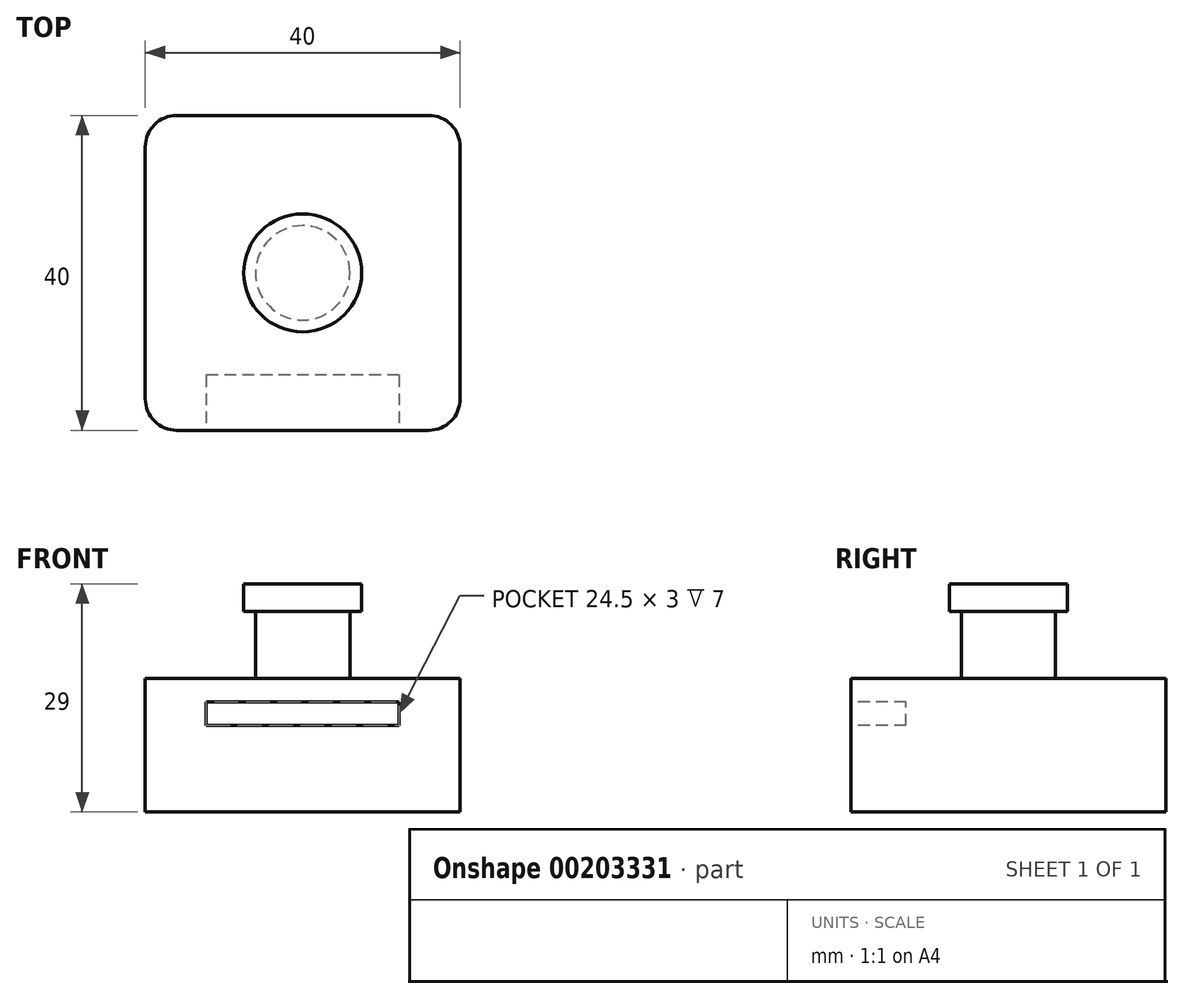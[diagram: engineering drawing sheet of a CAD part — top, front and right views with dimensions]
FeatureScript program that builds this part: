
annotation { "Feature Type Name" : "Feature", "Feature Type Description" : "" }
export const myFeature = defineFeature(function(context is Context, id is Id, definition is map)
    precondition{}
    {
        {
            var Q0;
            Q0=qCreatedBy(makeId("Top.planeOp"),FACE);
            var sketch = newSketch(context, id + "F0", { "sketchPlane" : qUnion([Q0])});
            skLineSegment(sketch, "E0.bottom", {"start": v(20, -20) * mm, "end": v(-20, -20) * mm});
            skLineSegment(sketch, "E0.top", {"start": v(20, 20) * mm, "end": v(-20, 20) * mm});
            skLineSegment(sketch, "E0.left", {"start": v(20, -20) * mm, "end": v(20, 20) * mm});
            skLineSegment(sketch, "E0.right", {"start": v(-20, -20) * mm, "end": v(-20, 20) * mm});
            skPoint(sketch, "E0.middle", {"position": v(0, 0) * mm});
            skSolve(sketch);
        }
        {
            var Q0;
            Q0 = qSketchRegion(id + "F0", true);
            extrude(context, id + "F1", {"entities" : qUnion([Q0]), "oppositeDirection" : true, "depth" : 17 * mm});
        }
        {
            var Q0;
            Q0=makeQuery(id+"F1.opExtrude","CAP_FACE",FACE,{"disambiguationData":[OSD([sQuery(id+"F0.wireOp",EDGE,"E0.bottom"),sQuery(id+"F0.wireOp",EDGE,"E0.top"),sQuery(id+"F0.wireOp",EDGE,"E0.left"),sQuery(id+"F0.wireOp",EDGE,"E0.right")])],"isStart":true});
            var sketch = newSketch(context, id + "F2", { "sketchPlane" : qUnion([Q0])});
            skCircle(sketch, "E1", {"center": v(0, 0) * mm, "radius": 6 * mm});
            skSolve(sketch);
        }
        {
            var Q0;
            Q0 = qSketchRegion(id + "F2", true);
            extrude(context, id + "F3", {"entities" : qUnion([Q0]), "operationType" : NewBodyOperationType.ADD, "depth" : 8.5 * mm});
        }
        {
            var Q0;
            Q0=makeQuery(id+"F3.opExtrude","CAP_FACE",FACE,{"disambiguationData":[OSD([sQuery(id+"F2.wireOp",EDGE,"E1")])],"isStart":false});
            var sketch = newSketch(context, id + "F4", { "sketchPlane" : qUnion([Q0])});
            skCircle(sketch, "E2", {"center": v(0, 0) * mm, "radius": 7.5 * mm});
            skSolve(sketch);
        }
        {
            var Q0;
            Q0 = qSketchRegion(id + "F4", true);
            extrude(context, id + "F5", {"entities" : qUnion([Q0]), "operationType" : NewBodyOperationType.ADD, "depth" : 3.5 * mm});
        }
        {
            var Q0;
            Q0=makeQuery(id+"F1.opExtrude","SWEPT_EDGE",EDGE,{"disambiguationData":[OSD([sQuery(id+"F0.wireOp",EDGE,"E0.bottom"),sQuery(id+"F0.wireOp",EDGE,"E0.left")])]});
            var Q1;
            Q1=makeQuery(id+"F1.opExtrude","SWEPT_EDGE",EDGE,{"disambiguationData":[OSD([sQuery(id+"F0.wireOp",EDGE,"E0.top"),sQuery(id+"F0.wireOp",EDGE,"E0.left")])]});
            var Q2;
            Q2=makeQuery(id+"F1.opExtrude","SWEPT_EDGE",EDGE,{"disambiguationData":[OSD([sQuery(id+"F0.wireOp",EDGE,"E0.top"),sQuery(id+"F0.wireOp",EDGE,"E0.right")])]});
            var Q3;
            Q3=makeQuery(id+"F1.opExtrude","SWEPT_EDGE",EDGE,{"disambiguationData":[OSD([sQuery(id+"F0.wireOp",EDGE,"E0.bottom"),sQuery(id+"F0.wireOp",EDGE,"E0.right")])]});
            fillet(context, id + "F6", {"entities" : qUnion([Q0, Q1, Q2, Q3]), "radius" : 4 * mm, "tangentPropagation" : true, "allowEdgeOverflow" : false});
        }
        {
            var Q0;
            Q0=makeQuery(id+"F1.opExtrude","SWEPT_FACE",FACE,{"disambiguationData":[OSD([sQuery(id+"F0.wireOp",EDGE,"E0.bottom")])]});
            var sketch = newSketch(context, id + "F7", { "sketchPlane" : qUnion([Q0])});
            skLineSegment(sketch, "E3", {"start": v(0, 0) * mm, "end": v(0, -17) * mm, "construction": true});
            skLineSegment(sketch, "E4", {"start": v(-16, -4.5) * mm, "end": v(16, -4.5) * mm, "construction": true});
            skLineSegment(sketch, "E5.bottom", {"start": v(12.25, -6) * mm, "end": v(-12.25, -6) * mm});
            skLineSegment(sketch, "E5.top", {"start": v(12.25, -3) * mm, "end": v(-12.25, -3) * mm});
            skLineSegment(sketch, "E5.left", {"start": v(12.25, -6) * mm, "end": v(12.25, -3) * mm});
            skLineSegment(sketch, "E5.right", {"start": v(-12.25, -6) * mm, "end": v(-12.25, -3) * mm});
            skPoint(sketch, "E5.middle", {"position": v(0, -4.5) * mm});
            skSolve(sketch);
        }
        {
            var Q0;
            Q0 = qSketchRegion(id + "F7", true);
            extrude(context, id + "F8", {"entities" : qUnion([Q0]), "operationType" : NewBodyOperationType.REMOVE, "oppositeDirection" : true, "depth" : 7 * mm});
        }
    });
